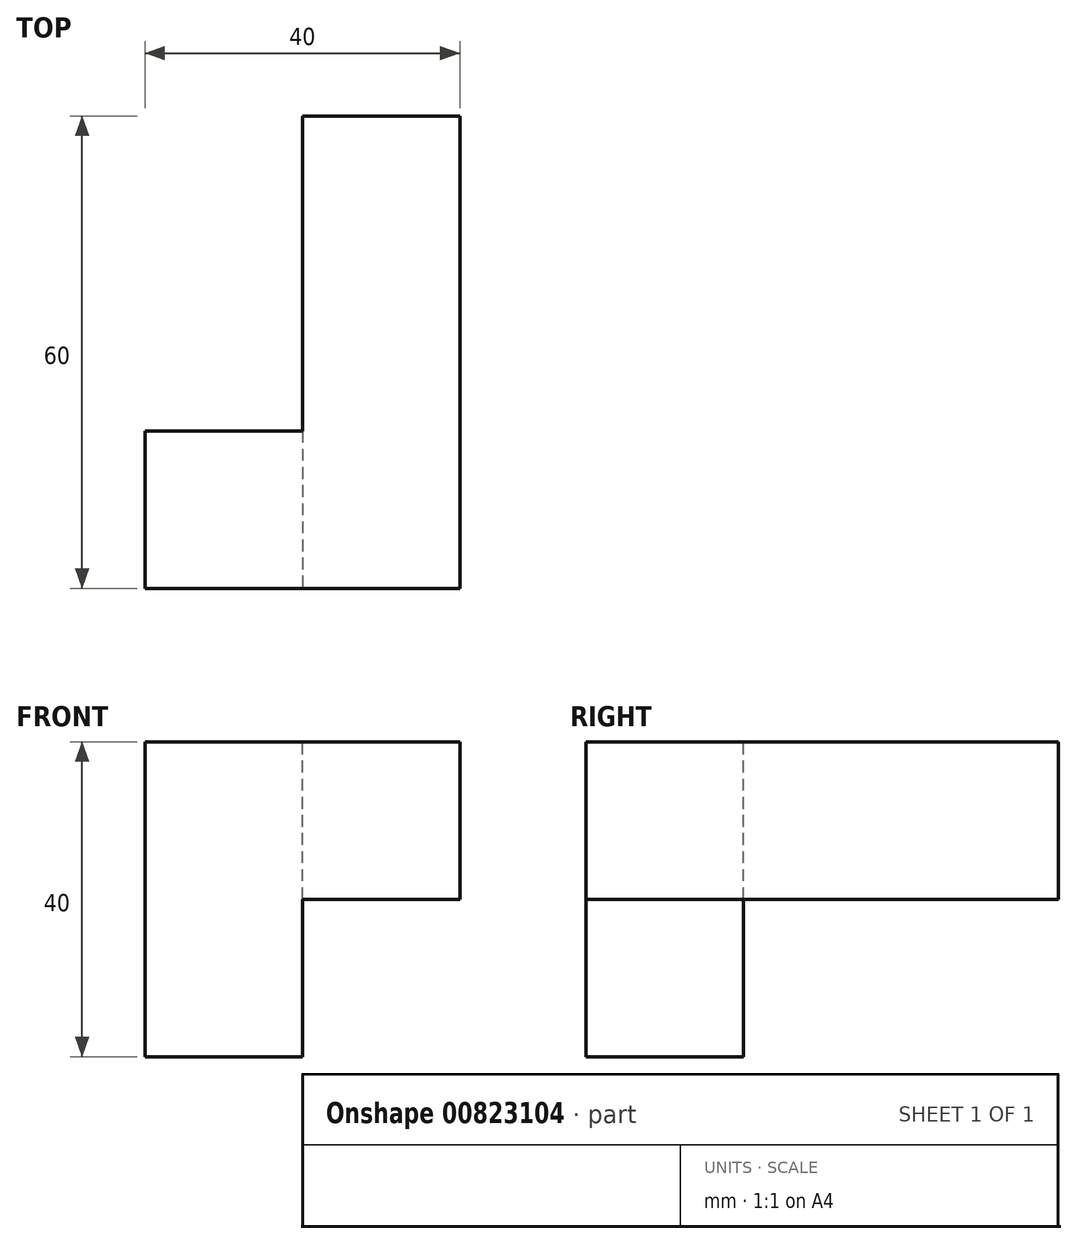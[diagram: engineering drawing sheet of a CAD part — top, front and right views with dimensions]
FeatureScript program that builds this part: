
annotation { "Feature Type Name" : "Feature", "Feature Type Description" : "" }
export const myFeature = defineFeature(function(context is Context, id is Id, definition is map)
    precondition{}
    {
        {
            var Q0;
            Q0=qCreatedBy(makeId("Front.planeOp"),FACE);
            var sketch = newSketch(context, id + "F0", { "sketchPlane" : qUnion([Q0])});
            skLineSegment(sketch, "E0.bottom", {"start": v(10, 10) * mm, "end": v(-10, 10) * mm});
            skLineSegment(sketch, "E0.top", {"start": v(10, -10) * mm, "end": v(-10, -10) * mm});
            skLineSegment(sketch, "E0.left", {"start": v(10, 10) * mm, "end": v(10, -10) * mm});
            skLineSegment(sketch, "E0.right", {"start": v(-10, 10) * mm, "end": v(-10, -10) * mm});
            skPoint(sketch, "E0.middle", {"position": v(0, 0) * mm});
            skSolve(sketch);
        }
        {
            var Q0;
            Q0 = qSketchRegion(id + "F0", true);
            extrude(context, id + "F1", {"entities" : qUnion([Q0]), "depth" : 60 * mm, "offsetDistance" : 25.4 * mm});
        }
        {
            var Q0;
            Q0=makeQuery(id+"F1.opExtrude","SWEPT_FACE",FACE,{"disambiguationData":[OSD([sQuery(id+"F0.wireOp",EDGE,"E0.right")])]});
            var sketch = newSketch(context, id + "F2", { "sketchPlane" : qUnion([Q0])});
            skLineSegment(sketch, "E1.bottom", {"start": v(60, -10) * mm, "end": v(40, -10) * mm});
            skLineSegment(sketch, "E1.top", {"start": v(60, 10) * mm, "end": v(40, 10) * mm});
            skLineSegment(sketch, "E1.left", {"start": v(60, -10) * mm, "end": v(60, 10) * mm});
            skLineSegment(sketch, "E1.right", {"start": v(40, -10) * mm, "end": v(40, 10) * mm});
            skSolve(sketch);
        }
        {
            var Q0;
            Q0 = qSketchRegion(id + "F2", true);
            extrude(context, id + "F3", {"entities" : qUnion([Q0]), "operationType" : NewBodyOperationType.ADD, "depth" : 20 * mm, "offsetDistance" : 25.4 * mm});
        }
        {
            var Q0;
            Q0=makeQuery(id+"F3.boolean.opBoolean","MERGE",FACE,{"derivedFrom":[makeQuery(id+"F1.opExtrude","SWEPT_FACE",FACE,{"disambiguationData":[OSD([sQuery(id+"F0.wireOp",EDGE,"E0.top")])]}),makeQuery(id+"F3.opExtrude","SWEPT_FACE",FACE,{"disambiguationData":[OSD([sQuery(id+"F2.wireOp",EDGE,"E1.bottom")])]})]});
            var sketch = newSketch(context, id + "F4", { "sketchPlane" : qUnion([Q0])});
            skLineSegment(sketch, "E2", {"start": v(-10, 40) * mm, "end": v(-10, 60) * mm});
            skSolve(sketch);
        }
        {
            var Q0;
            {var subQ0=sQuery(id+"F4.wireOp",EDGE,"E2");Q0=makeQuery(id+"F4.imprint","IMPRINT",FACE,{"disambiguationData":[TD([[makeQuery(id+"F4.imprint","IMPRINT",EDGE,{"derivedFrom":subQ0}),1.0]])]});}
            extrude(context, id + "F5", {"entities" : qUnion([Q0]), "operationType" : NewBodyOperationType.ADD, "depth" : 20 * mm, "offsetDistance" : 25.4 * mm});
        }
    });
